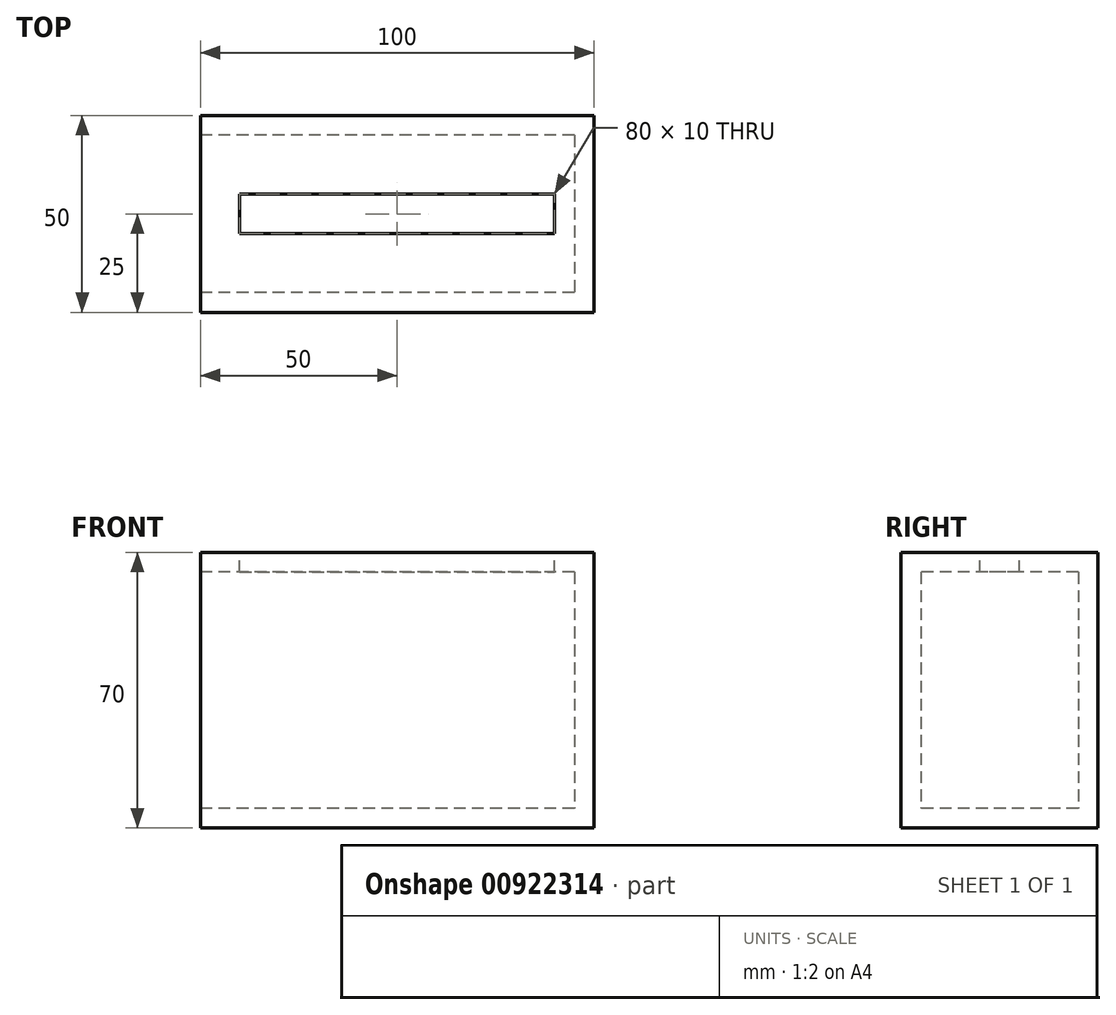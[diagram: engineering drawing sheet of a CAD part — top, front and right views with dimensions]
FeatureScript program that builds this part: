
annotation { "Feature Type Name" : "Feature", "Feature Type Description" : "" }
export const myFeature = defineFeature(function(context is Context, id is Id, definition is map)
    precondition{}
    {
        {
            var Q0;
            Q0=qCreatedBy(makeId("Top.planeOp"),FACE);
            var sketch = newSketch(context, id + "F0", { "sketchPlane" : qUnion([Q0])});
            skLineSegment(sketch, "E0.bottom", {"start": v(0, 0) * mm, "end": v(-100, 0) * mm});
            skLineSegment(sketch, "E0.top", {"start": v(0, 50) * mm, "end": v(-100, 50) * mm});
            skLineSegment(sketch, "E0.left", {"start": v(0, 0) * mm, "end": v(0, 50) * mm});
            skLineSegment(sketch, "E0.right", {"start": v(-100, 0) * mm, "end": v(-100, 50) * mm});
            skSolve(sketch);
        }
        {
            var Q0;
            Q0 = qSketchRegion(id + "F0", true);
            extrude(context, id + "F1", {"entities" : qUnion([Q0]), "endBound" : BoundingType.SYMMETRIC, "depth" : 70 * mm, "offsetDistance" : 25 * mm});
        }
        {
            var Q0;
            Q0=makeQuery(id+"F1.opExtrude","SWEPT_FACE",FACE,{"disambiguationData":[OSD([sQuery(id+"F0.wireOp",EDGE,"E0.right")])]});
            var sketch = newSketch(context, id + "F2", { "sketchPlane" : qUnion([Q0])});
            skLineSegment(sketch, "E1.bottom", {"start": v(-45, 30) * mm, "end": v(-5, 30) * mm});
            skLineSegment(sketch, "E1.top", {"start": v(-45, -30) * mm, "end": v(-5, -30) * mm});
            skLineSegment(sketch, "E1.left", {"start": v(-45, 30) * mm, "end": v(-45, -30) * mm});
            skLineSegment(sketch, "E1.right", {"start": v(-5, 30) * mm, "end": v(-5, -30) * mm});
            skSolve(sketch);
        }
        {
            var Q0;
            Q0 = qSketchRegion(id + "F2", true);
            extrude(context, id + "F3", {"entities" : qUnion([Q0]), "operationType" : NewBodyOperationType.REMOVE, "oppositeDirection" : true, "depth" : 95 * mm, "offsetDistance" : 25 * mm});
        }
        {
            var Q0;
            Q0=makeQuery(id+"F1.opExtrude","CAP_FACE",FACE,{"disambiguationData":[OSD([sQuery(id+"F0.wireOp",EDGE,"E0.bottom"),sQuery(id+"F0.wireOp",EDGE,"E0.top"),sQuery(id+"F0.wireOp",EDGE,"E0.left"),sQuery(id+"F0.wireOp",EDGE,"E0.right")])],"isStart":false});
            var sketch = newSketch(context, id + "F4", { "sketchPlane" : qUnion([Q0])});
            skLineSegment(sketch, "E2.bottom", {"start": v(-90, 30) * mm, "end": v(-10, 30) * mm});
            skLineSegment(sketch, "E2.top", {"start": v(-90, 20) * mm, "end": v(-10, 20) * mm});
            skLineSegment(sketch, "E2.left", {"start": v(-90, 30) * mm, "end": v(-90, 20) * mm});
            skLineSegment(sketch, "E2.right", {"start": v(-10, 30) * mm, "end": v(-10, 20) * mm});
            skSolve(sketch);
        }
        {
            var Q0;
            Q0 = qSketchRegion(id + "F4", true);
            var Q1;
            Q1=makeQuery(id+"F3.boolean.opBoolean","COPY",FACE,{"derivedFrom":makeQuery(id+"F3.opExtrude","SWEPT_FACE",FACE,{"disambiguationData":[OSD([sQuery(id+"F2.wireOp",EDGE,"E1.bottom")])]})});
            extrude(context, id + "F5", {"entities" : qUnion([Q0]), "operationType" : NewBodyOperationType.REMOVE, "endBound" : BoundingType.UP_TO_SURFACE, "oppositeDirection" : true, "depth" : 25 * mm, "endBoundEntityFace" : qUnion([Q1]), "offsetDistance" : 25 * mm});
        }
    });
